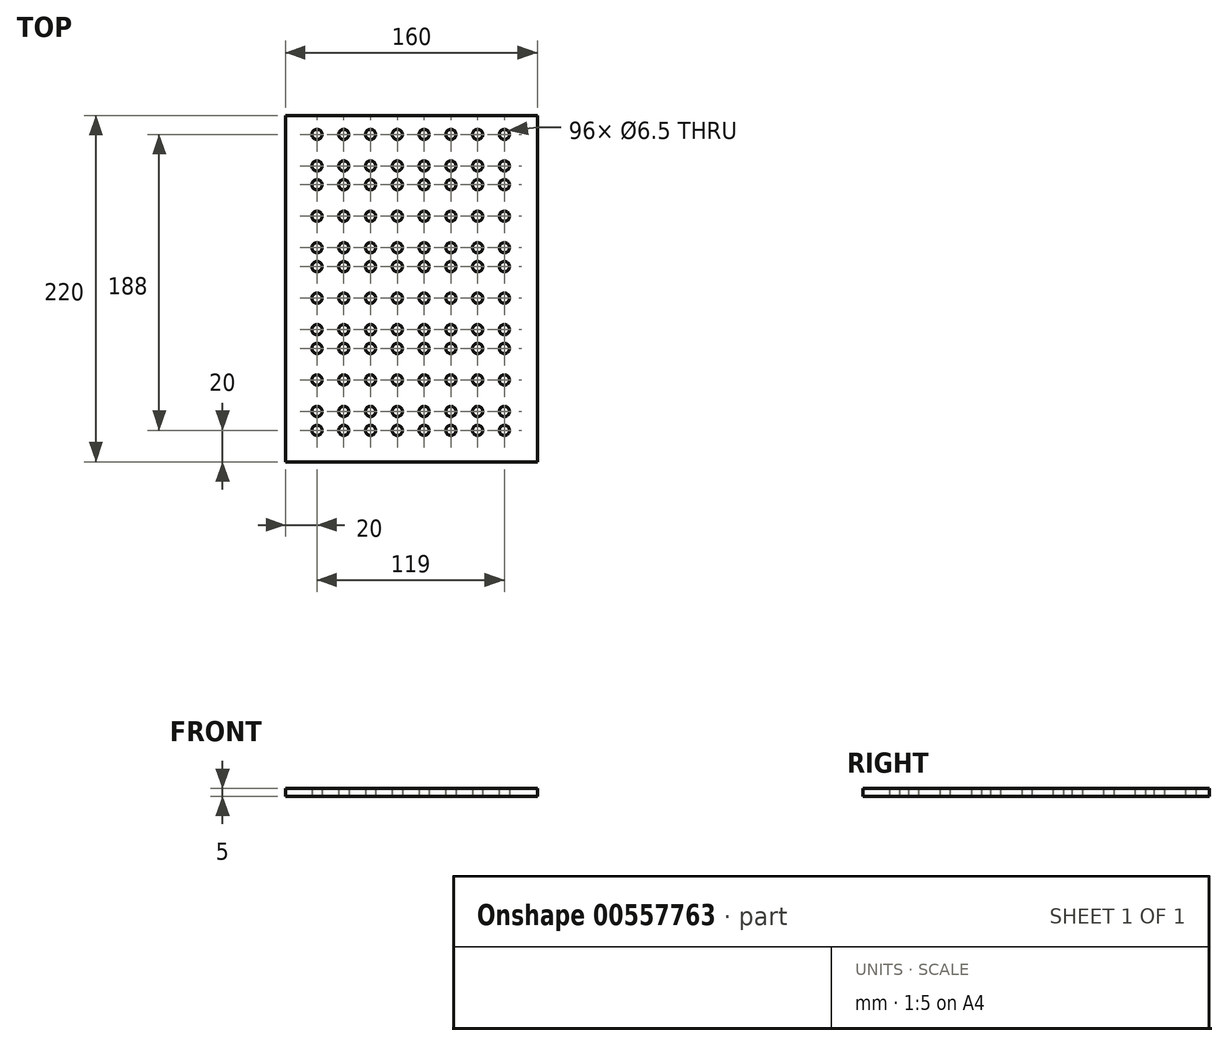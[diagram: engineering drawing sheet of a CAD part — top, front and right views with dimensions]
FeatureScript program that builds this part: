
annotation { "Feature Type Name" : "Feature", "Feature Type Description" : "" }
export const myFeature = defineFeature(function(context is Context, id is Id, definition is map)
    precondition{}
    {
        {
            var Q0;
            Q0=qCreatedBy(makeId("Top.planeOp"),FACE);
            var sketch = newSketch(context, id + "F0", { "sketchPlane" : qUnion([Q0])});
            skLineSegment(sketch, "E0.bottom", {"start": v(-80, 110) * mm, "end": v(80, 110) * mm});
            skLineSegment(sketch, "E0.top", {"start": v(-80, -110) * mm, "end": v(80, -110) * mm});
            skLineSegment(sketch, "E0.left", {"start": v(-80, 110) * mm, "end": v(-80, -110) * mm});
            skLineSegment(sketch, "E0.right", {"start": v(80, 110) * mm, "end": v(80, -110) * mm});
            skCircle(sketch, "E1", {"center": v(-60, -90) * mm, "radius": 3.25 * mm});
            skCircle(sketch, "E2.0.1.0", {"center": v(-60, -78) * mm, "radius": 3.25 * mm});
            skCircle(sketch, "E2.1.0.0", {"center": v(-43, -90) * mm, "radius": 3.25 * mm});
            skCircle(sketch, "E2.1.1.0", {"center": v(-43, -78) * mm, "radius": 3.25 * mm});
            skCircle(sketch, "E2.2.0.0", {"center": v(-26, -90) * mm, "radius": 3.25 * mm});
            skCircle(sketch, "E2.2.1.0", {"center": v(-26, -78) * mm, "radius": 3.25 * mm});
            skCircle(sketch, "E2.3.0.0", {"center": v(-9, -90) * mm, "radius": 3.25 * mm});
            skCircle(sketch, "E2.3.1.0", {"center": v(-9, -78) * mm, "radius": 3.25 * mm});
            skCircle(sketch, "E2.4.0.0", {"center": v(8, -90) * mm, "radius": 3.25 * mm});
            skCircle(sketch, "E2.4.1.0", {"center": v(8, -78) * mm, "radius": 3.25 * mm});
            skCircle(sketch, "E2.5.0.0", {"center": v(25, -90) * mm, "radius": 3.25 * mm});
            skCircle(sketch, "E2.5.1.0", {"center": v(25, -78) * mm, "radius": 3.25 * mm});
            skCircle(sketch, "E2.6.0.0", {"center": v(42, -90) * mm, "radius": 3.25 * mm});
            skCircle(sketch, "E2.6.1.0", {"center": v(42, -78) * mm, "radius": 3.25 * mm});
            skCircle(sketch, "E2.7.0.0", {"center": v(59, -90) * mm, "radius": 3.25 * mm});
            skCircle(sketch, "E2.7.1.0", {"center": v(59, -78) * mm, "radius": 3.25 * mm});
            skLineSegment(sketch, "E2.direction1", {"start": v(-60, -90) * mm, "end": v(-43, -90) * mm, "construction": true});
            skLineSegment(sketch, "E2.direction2", {"start": v(-60, -90) * mm, "end": v(-60, -78) * mm, "construction": true});
            skCircle(sketch, "E3", {"center": v(-60, -58) * mm, "radius": 3.25 * mm});
            skCircle(sketch, "E4.1.0.0", {"center": v(-43, -58) * mm, "radius": 3.25 * mm});
            skCircle(sketch, "E4.2.0.0", {"center": v(-26, -58) * mm, "radius": 3.25 * mm});
            skCircle(sketch, "E4.3.0.0", {"center": v(-9, -58) * mm, "radius": 3.25 * mm});
            skCircle(sketch, "E4.4.0.0", {"center": v(8, -58) * mm, "radius": 3.25 * mm});
            skCircle(sketch, "E4.5.0.0", {"center": v(25, -58) * mm, "radius": 3.25 * mm});
            skCircle(sketch, "E4.6.0.0", {"center": v(42, -58) * mm, "radius": 3.25 * mm});
            skCircle(sketch, "E4.7.0.0", {"center": v(59, -58) * mm, "radius": 3.25 * mm});
            skLineSegment(sketch, "E4.direction1", {"start": v(-60, -58) * mm, "end": v(-43, -58) * mm, "construction": true});
            skCircle(sketch, "E5", {"center": v(-60, -38) * mm, "radius": 3.25 * mm});
            skCircle(sketch, "E6.0.1.0", {"center": v(-60, -26) * mm, "radius": 3.25 * mm});
            skCircle(sketch, "E6.1.0.0", {"center": v(-43, -38) * mm, "radius": 3.25 * mm});
            skCircle(sketch, "E6.1.1.0", {"center": v(-43, -26) * mm, "radius": 3.25 * mm});
            skCircle(sketch, "E6.2.0.0", {"center": v(-26, -38) * mm, "radius": 3.25 * mm});
            skCircle(sketch, "E6.2.1.0", {"center": v(-26, -26) * mm, "radius": 3.25 * mm});
            skCircle(sketch, "E6.3.0.0", {"center": v(-9, -38) * mm, "radius": 3.25 * mm});
            skCircle(sketch, "E6.3.1.0", {"center": v(-9, -26) * mm, "radius": 3.25 * mm});
            skCircle(sketch, "E6.4.0.0", {"center": v(8, -38) * mm, "radius": 3.25 * mm});
            skCircle(sketch, "E6.4.1.0", {"center": v(8, -26) * mm, "radius": 3.25 * mm});
            skCircle(sketch, "E6.5.0.0", {"center": v(25, -38) * mm, "radius": 3.25 * mm});
            skCircle(sketch, "E6.5.1.0", {"center": v(25, -26) * mm, "radius": 3.25 * mm});
            skCircle(sketch, "E6.6.0.0", {"center": v(42, -38) * mm, "radius": 3.25 * mm});
            skCircle(sketch, "E6.6.1.0", {"center": v(42, -26) * mm, "radius": 3.25 * mm});
            skCircle(sketch, "E6.7.0.0", {"center": v(59, -38) * mm, "radius": 3.25 * mm});
            skCircle(sketch, "E6.7.1.0", {"center": v(59, -26) * mm, "radius": 3.25 * mm});
            skLineSegment(sketch, "E6.direction1", {"start": v(-60, -38) * mm, "end": v(-43, -38) * mm, "construction": true});
            skLineSegment(sketch, "E6.direction2", {"start": v(-60, -38) * mm, "end": v(-60, -26) * mm, "construction": true});
            skCircle(sketch, "E7", {"center": v(-60, -6) * mm, "radius": 3.25 * mm});
            skCircle(sketch, "E8.1.0.0", {"center": v(-43, -6) * mm, "radius": 3.25 * mm});
            skCircle(sketch, "E8.2.0.0", {"center": v(-26, -6) * mm, "radius": 3.25 * mm});
            skCircle(sketch, "E8.3.0.0", {"center": v(-9, -6) * mm, "radius": 3.25 * mm});
            skCircle(sketch, "E8.4.0.0", {"center": v(8, -6) * mm, "radius": 3.25 * mm});
            skCircle(sketch, "E8.5.0.0", {"center": v(25, -6) * mm, "radius": 3.25 * mm});
            skCircle(sketch, "E8.6.0.0", {"center": v(42, -6) * mm, "radius": 3.25 * mm});
            skCircle(sketch, "E8.7.0.0", {"center": v(59, -6) * mm, "radius": 3.25 * mm});
            skLineSegment(sketch, "E8.direction1", {"start": v(-60, -6) * mm, "end": v(-43, -6) * mm, "construction": true});
            skCircle(sketch, "E9", {"center": v(-60, 14) * mm, "radius": 3.25 * mm});
            skCircle(sketch, "E10.0.1.0", {"center": v(-60, 26) * mm, "radius": 3.25 * mm});
            skCircle(sketch, "E10.1.0.0", {"center": v(-43, 14) * mm, "radius": 3.25 * mm});
            skCircle(sketch, "E10.1.1.0", {"center": v(-43, 26) * mm, "radius": 3.25 * mm});
            skCircle(sketch, "E10.2.0.0", {"center": v(-26, 14) * mm, "radius": 3.25 * mm});
            skCircle(sketch, "E10.2.1.0", {"center": v(-26, 26) * mm, "radius": 3.25 * mm});
            skCircle(sketch, "E10.3.0.0", {"center": v(-9, 14) * mm, "radius": 3.25 * mm});
            skCircle(sketch, "E10.3.1.0", {"center": v(-9, 26) * mm, "radius": 3.25 * mm});
            skCircle(sketch, "E10.4.0.0", {"center": v(8, 14) * mm, "radius": 3.25 * mm});
            skCircle(sketch, "E10.4.1.0", {"center": v(8, 26) * mm, "radius": 3.25 * mm});
            skCircle(sketch, "E10.5.0.0", {"center": v(25, 14) * mm, "radius": 3.25 * mm});
            skCircle(sketch, "E10.5.1.0", {"center": v(25, 26) * mm, "radius": 3.25 * mm});
            skCircle(sketch, "E10.6.0.0", {"center": v(42, 14) * mm, "radius": 3.25 * mm});
            skCircle(sketch, "E10.6.1.0", {"center": v(42, 26) * mm, "radius": 3.25 * mm});
            skCircle(sketch, "E10.7.0.0", {"center": v(59, 14) * mm, "radius": 3.25 * mm});
            skCircle(sketch, "E10.7.1.0", {"center": v(59, 26) * mm, "radius": 3.25 * mm});
            skLineSegment(sketch, "E10.direction1", {"start": v(-60, 14) * mm, "end": v(-43, 14) * mm, "construction": true});
            skLineSegment(sketch, "E10.direction2", {"start": v(-60, 14) * mm, "end": v(-60, 26) * mm, "construction": true});
            skCircle(sketch, "E11", {"center": v(-60, 46) * mm, "radius": 3.25 * mm});
            skCircle(sketch, "E12.1.0.0", {"center": v(-43, 46) * mm, "radius": 3.25 * mm});
            skCircle(sketch, "E12.2.0.0", {"center": v(-26, 46) * mm, "radius": 3.25 * mm});
            skCircle(sketch, "E12.3.0.0", {"center": v(-9, 46) * mm, "radius": 3.25 * mm});
            skCircle(sketch, "E12.4.0.0", {"center": v(8, 46) * mm, "radius": 3.25 * mm});
            skCircle(sketch, "E12.5.0.0", {"center": v(25, 46) * mm, "radius": 3.25 * mm});
            skCircle(sketch, "E12.6.0.0", {"center": v(42, 46) * mm, "radius": 3.25 * mm});
            skCircle(sketch, "E12.7.0.0", {"center": v(59, 46) * mm, "radius": 3.25 * mm});
            skLineSegment(sketch, "E12.direction1", {"start": v(-60, 46) * mm, "end": v(-43, 46) * mm, "construction": true});
            skCircle(sketch, "E13", {"center": v(-60, 66) * mm, "radius": 3.25 * mm});
            skCircle(sketch, "E14.0.1.0", {"center": v(-60, 78) * mm, "radius": 3.25 * mm});
            skCircle(sketch, "E14.1.0.0", {"center": v(-43, 66) * mm, "radius": 3.25 * mm});
            skCircle(sketch, "E14.1.1.0", {"center": v(-43, 78) * mm, "radius": 3.25 * mm});
            skCircle(sketch, "E14.2.0.0", {"center": v(-26, 66) * mm, "radius": 3.25 * mm});
            skCircle(sketch, "E14.2.1.0", {"center": v(-26, 78) * mm, "radius": 3.25 * mm});
            skCircle(sketch, "E14.3.0.0", {"center": v(-9, 66) * mm, "radius": 3.25 * mm});
            skCircle(sketch, "E14.3.1.0", {"center": v(-9, 78) * mm, "radius": 3.25 * mm});
            skCircle(sketch, "E14.4.0.0", {"center": v(8, 66) * mm, "radius": 3.25 * mm});
            skCircle(sketch, "E14.4.1.0", {"center": v(8, 78) * mm, "radius": 3.25 * mm});
            skCircle(sketch, "E14.5.0.0", {"center": v(25, 66) * mm, "radius": 3.25 * mm});
            skCircle(sketch, "E14.5.1.0", {"center": v(25, 78) * mm, "radius": 3.25 * mm});
            skCircle(sketch, "E14.6.0.0", {"center": v(42, 66) * mm, "radius": 3.25 * mm});
            skCircle(sketch, "E14.6.1.0", {"center": v(42, 78) * mm, "radius": 3.25 * mm});
            skCircle(sketch, "E14.7.0.0", {"center": v(59, 66) * mm, "radius": 3.25 * mm});
            skCircle(sketch, "E14.7.1.0", {"center": v(59, 78) * mm, "radius": 3.25 * mm});
            skLineSegment(sketch, "E14.direction1", {"start": v(-60, 66) * mm, "end": v(-43, 66) * mm, "construction": true});
            skLineSegment(sketch, "E14.direction2", {"start": v(-60, 66) * mm, "end": v(-60, 78) * mm, "construction": true});
            skCircle(sketch, "E15", {"center": v(-60, 98) * mm, "radius": 3.25 * mm});
            skCircle(sketch, "E16.1.0.0", {"center": v(-43, 98) * mm, "radius": 3.25 * mm});
            skCircle(sketch, "E16.2.0.0", {"center": v(-26, 98) * mm, "radius": 3.25 * mm});
            skCircle(sketch, "E16.3.0.0", {"center": v(-9, 98) * mm, "radius": 3.25 * mm});
            skCircle(sketch, "E16.4.0.0", {"center": v(8, 98) * mm, "radius": 3.25 * mm});
            skCircle(sketch, "E16.5.0.0", {"center": v(25, 98) * mm, "radius": 3.25 * mm});
            skCircle(sketch, "E16.6.0.0", {"center": v(42, 98) * mm, "radius": 3.25 * mm});
            skCircle(sketch, "E16.7.0.0", {"center": v(59, 98) * mm, "radius": 3.25 * mm});
            skLineSegment(sketch, "E16.direction1", {"start": v(-60, 98) * mm, "end": v(-43, 98) * mm, "construction": true});
            skSolve(sketch);
        }
        {
            var Q0;
            Q0 = qSketchRegion(id + "F0", true);
            extrude(context, id + "F1", {"entities" : qUnion([Q0]), "depth" : 5 * mm, "offsetDistance" : 25 * mm});
        }
    });
